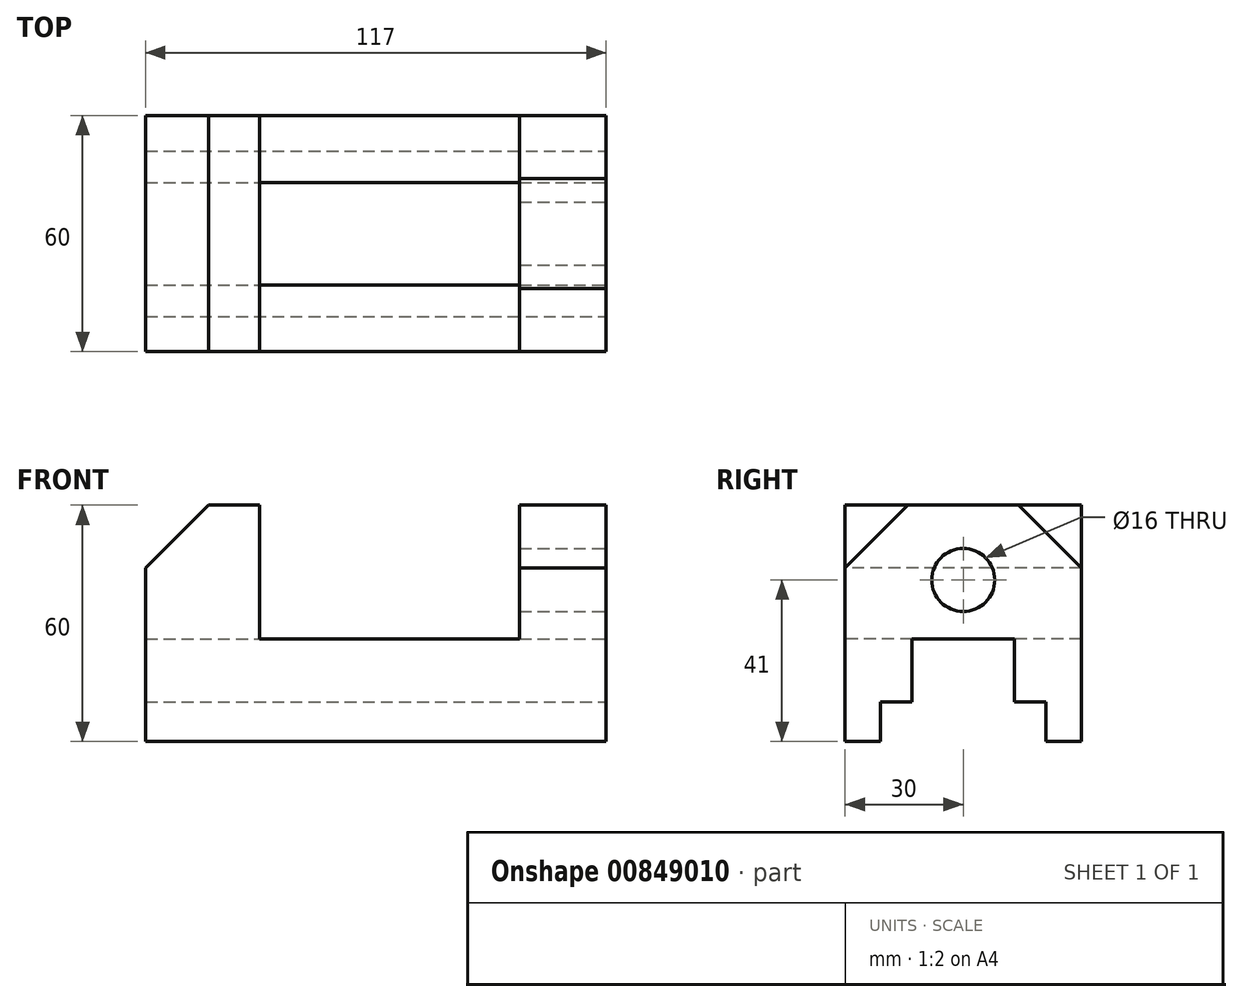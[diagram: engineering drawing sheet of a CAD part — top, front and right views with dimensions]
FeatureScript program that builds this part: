
annotation { "Feature Type Name" : "Feature", "Feature Type Description" : "" }
export const myFeature = defineFeature(function(context is Context, id is Id, definition is map)
    precondition{}
    {
        {
            var Q0;
            Q0=qCreatedBy(makeId("Front.planeOp"),FACE);
            var sketch = newSketch(context, id + "F0", { "sketchPlane" : qUnion([Q0])});
            skLineSegment(sketch, "E0.bottom", {"start": v(0, 0) * mm, "end": v(-117, 0) * mm});
            skLineSegment(sketch, "E0.top", {"start": v(0, 60) * mm, "end": v(-117, 60) * mm});
            skLineSegment(sketch, "E0.left", {"start": v(0, 0) * mm, "end": v(0, 60) * mm});
            skLineSegment(sketch, "E0.right", {"start": v(-117, 0) * mm, "end": v(-117, 60) * mm});
            skSolve(sketch);
        }
        {
            var Q0;
            Q0 = qSketchRegion(id + "F0", true);
            extrude(context, id + "F1", {"entities" : qUnion([Q0]), "depth" : 60 * mm, "offsetDistance" : 25.4 * mm});
        }
        {
            var Q0;
            Q0=makeQuery(id+"F1.opExtrude","SWEPT_FACE",FACE,{"disambiguationData":[OSD([sQuery(id+"F0.wireOp",EDGE,"E0.left")])]});
            var sketch = newSketch(context, id + "F2", { "sketchPlane" : qUnion([Q0])});
            skLineSegment(sketch, "E1", {"start": v(-60, 0) * mm, "end": v(-51, 0) * mm});
            skLineSegment(sketch, "E2", {"start": v(0, 0) * mm, "end": v(-9, 0) * mm});
            skLineSegment(sketch, "E3", {"start": v(-9, 0) * mm, "end": v(-9, 10) * mm});
            skLineSegment(sketch, "E4", {"start": v(-9, 10) * mm, "end": v(-51, 10) * mm});
            skLineSegment(sketch, "E5", {"start": v(-51, 10) * mm, "end": v(-51, 0) * mm});
            skLineSegment(sketch, "E6", {"start": v(-51, 0) * mm, "end": v(-9, 0) * mm});
            skSolve(sketch);
        }
        {
            var Q0;
            Q0 = qSketchRegion(id + "F2", true);
            extrude(context, id + "F3", {"entities" : qUnion([Q0]), "operationType" : NewBodyOperationType.REMOVE, "oppositeDirection" : true, "depth" : 117 * mm, "offsetDistance" : 25.4 * mm});
        }
        {
            var Q0;
            Q0=makeQuery(id+"F1.opExtrude","SWEPT_FACE",FACE,{"disambiguationData":[OSD([sQuery(id+"F0.wireOp",EDGE,"E0.left")])]});
            var sketch = newSketch(context, id + "F4", { "sketchPlane" : qUnion([Q0])});
            skLineSegment(sketch, "E7", {"start": v(-51, 10) * mm, "end": v(-43, 10) * mm});
            skLineSegment(sketch, "E8", {"start": v(-9, 10) * mm, "end": v(-17, 10) * mm});
            skLineSegment(sketch, "E9", {"start": v(-17, 10) * mm, "end": v(-17, 26) * mm});
            skLineSegment(sketch, "E10", {"start": v(-43, 10) * mm, "end": v(-43, 26) * mm});
            skLineSegment(sketch, "E11", {"start": v(-43, 26) * mm, "end": v(-17, 26) * mm});
            skLineSegment(sketch, "E12", {"start": v(-43, 10) * mm, "end": v(-17, 10) * mm});
            skSolve(sketch);
        }
        {
            var Q0;
            Q0 = qSketchRegion(id + "F4", true);
            extrude(context, id + "F5", {"entities" : qUnion([Q0]), "operationType" : NewBodyOperationType.REMOVE, "oppositeDirection" : true, "depth" : 117 * mm, "offsetDistance" : 25.4 * mm});
        }
        {
            var Q0;
            Q0=makeQuery(id+"F1.opExtrude","SWEPT_FACE",FACE,{"disambiguationData":[OSD([sQuery(id+"F0.wireOp",EDGE,"E0.left")])]});
            var sketch = newSketch(context, id + "F6", { "sketchPlane" : qUnion([Q0])});
            skLineSegment(sketch, "E13", {"start": v(-60, 0) * mm, "end": v(-60, 41) * mm});
            skLineSegment(sketch, "E14", {"start": v(-43, 26) * mm, "end": v(-30, 26) * mm});
            skLineSegment(sketch, "E15", {"start": v(-60, 41) * mm, "end": v(-30, 41) * mm});
            skCircle(sketch, "E16", {"center": v(-30, 41) * mm, "radius": 8 * mm});
            skSolve(sketch);
        }
        {
            var Q0;
            Q0 = qSketchRegion(id + "F6", true);
            extrude(context, id + "F7", {"entities" : qUnion([Q0]), "operationType" : NewBodyOperationType.REMOVE, "oppositeDirection" : true, "depth" : 22 * mm, "offsetDistance" : 25.4 * mm});
        }
        {
            var Q0;
            Q0=makeQuery(id+"F1.opExtrude","SWEPT_FACE",FACE,{"disambiguationData":[OSD([sQuery(id+"F0.wireOp",EDGE,"E0.left")])]});
            var sketch = newSketch(context, id + "F8", { "sketchPlane" : qUnion([Q0])});
            skLineSegment(sketch, "E17", {"start": v(0, 60) * mm, "end": v(-16, 60) * mm});
            skLineSegment(sketch, "E18", {"start": v(-60, 60) * mm, "end": v(-44, 60) * mm});
            skLineSegment(sketch, "E19", {"start": v(-44, 60) * mm, "end": v(-60, 44) * mm});
            skLineSegment(sketch, "E20", {"start": v(-60, 60) * mm, "end": v(-60, 44) * mm});
            skSolve(sketch);
        }
        {
            var Q0;
            Q0 = qSketchRegion(id + "F8", true);
            extrude(context, id + "F9", {"entities" : qUnion([Q0]), "operationType" : NewBodyOperationType.REMOVE, "oppositeDirection" : true, "depth" : 22 * mm, "offsetDistance" : 25.4 * mm});
        }
        {
            var Q0;
            Q0=makeQuery(id+"F1.opExtrude","SWEPT_FACE",FACE,{"disambiguationData":[OSD([sQuery(id+"F0.wireOp",EDGE,"E0.left")])]});
            var sketch = newSketch(context, id + "F10", { "sketchPlane" : qUnion([Q0])});
            skLineSegment(sketch, "E21", {"start": v(0, 60) * mm, "end": v(-16, 60) * mm});
            skLineSegment(sketch, "E22", {"start": v(-16, 60) * mm, "end": v(0, 44) * mm});
            skLineSegment(sketch, "E23", {"start": v(0, 60) * mm, "end": v(0, 44) * mm});
            skSolve(sketch);
        }
        {
            var Q0;
            Q0 = qSketchRegion(id + "F10", true);
            extrude(context, id + "F11", {"entities" : qUnion([Q0]), "operationType" : NewBodyOperationType.REMOVE, "oppositeDirection" : true, "depth" : 22 * mm, "offsetDistance" : 25.4 * mm});
        }
        {
            var Q0;
            Q0=makeQuery(id+"F1.opExtrude","CAP_FACE",FACE,{"disambiguationData":[OSD([sQuery(id+"F0.wireOp",EDGE,"E0.bottom"),sQuery(id+"F0.wireOp",EDGE,"E0.top"),sQuery(id+"F0.wireOp",EDGE,"E0.left"),sQuery(id+"F0.wireOp",EDGE,"E0.right")])],"isStart":false});
            var sketch = newSketch(context, id + "F12", { "sketchPlane" : qUnion([Q0])});
            skLineSegment(sketch, "E24", {"start": v(-22, 0) * mm, "end": v(-22, 26) * mm});
            skLineSegment(sketch, "E25", {"start": v(-117, 60) * mm, "end": v(-88, 60) * mm});
            skLineSegment(sketch, "E26", {"start": v(-88, 60) * mm, "end": v(-88, 26) * mm});
            skLineSegment(sketch, "E27", {"start": v(-88, 26) * mm, "end": v(-22, 26) * mm});
            skLineSegment(sketch, "E28", {"start": v(-22, 26) * mm, "end": v(-22, 44) * mm});
            skLineSegment(sketch, "E29", {"start": v(-22, 44) * mm, "end": v(-22, 60) * mm});
            skLineSegment(sketch, "E30", {"start": v(-22, 60) * mm, "end": v(-88, 60) * mm});
            skSolve(sketch);
        }
        {
            var Q0;
            Q0 = qSketchRegion(id + "F12", true);
            extrude(context, id + "F13", {"entities" : qUnion([Q0]), "operationType" : NewBodyOperationType.REMOVE, "oppositeDirection" : true, "depth" : 60 * mm, "offsetDistance" : 25.4 * mm});
        }
        {
            var Q0;
            Q0=makeQuery(id+"F1.opExtrude","CAP_FACE",FACE,{"disambiguationData":[OSD([sQuery(id+"F0.wireOp",EDGE,"E0.bottom"),sQuery(id+"F0.wireOp",EDGE,"E0.top"),sQuery(id+"F0.wireOp",EDGE,"E0.left"),sQuery(id+"F0.wireOp",EDGE,"E0.right")])],"isStart":false});
            var sketch = newSketch(context, id + "F14", { "sketchPlane" : qUnion([Q0])});
            skLineSegment(sketch, "E31", {"start": v(-117, 60) * mm, "end": v(-117, 44) * mm});
            skLineSegment(sketch, "E32", {"start": v(-117, 44) * mm, "end": v(-101, 60) * mm});
            skLineSegment(sketch, "E33", {"start": v(-117, 60) * mm, "end": v(-101, 60) * mm});
            skSolve(sketch);
        }
        {
            var Q0;
            Q0 = qSketchRegion(id + "F14", true);
            extrude(context, id + "F15", {"entities" : qUnion([Q0]), "operationType" : NewBodyOperationType.REMOVE, "oppositeDirection" : true, "depth" : 60 * mm, "offsetDistance" : 25.4 * mm});
        }
    });
